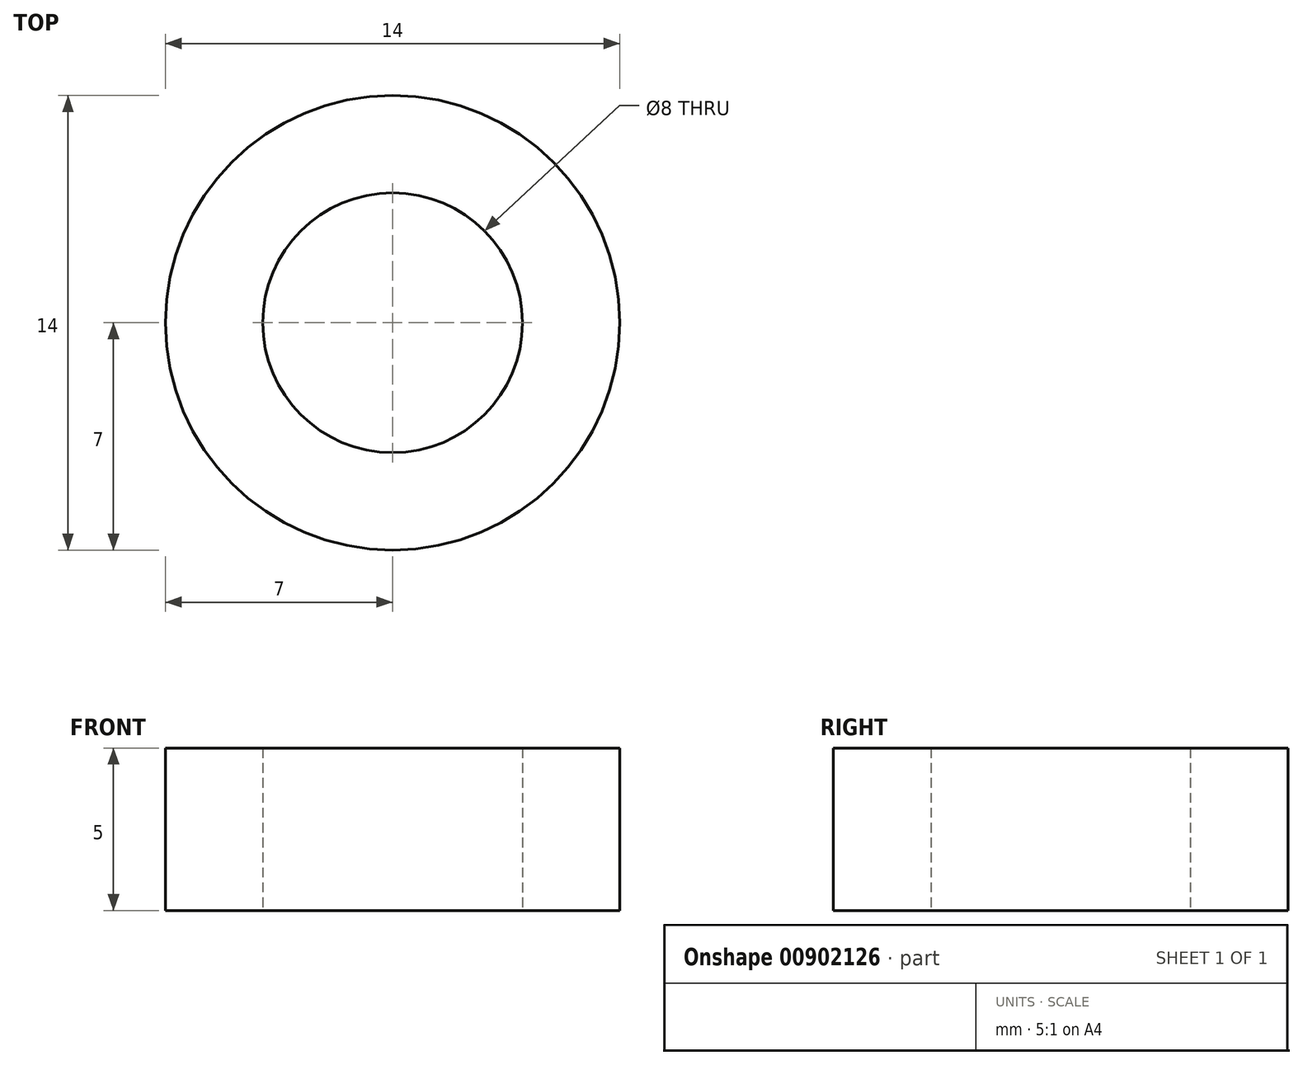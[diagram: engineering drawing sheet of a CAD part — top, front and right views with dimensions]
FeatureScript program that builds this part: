
annotation { "Feature Type Name" : "Feature", "Feature Type Description" : "" }
export const myFeature = defineFeature(function(context is Context, id is Id, definition is map)
    precondition{}
    {
        {
            var Q0;
            Q0=qCreatedBy(makeId("Top.planeOp"),FACE);
            var sketch = newSketch(context, id + "F0", { "sketchPlane" : qUnion([Q0])});
            skCircle(sketch, "E0", {"center": v(0, 0) * mm, "radius": 7 * mm});
            skCircle(sketch, "E1", {"center": v(0, 0) * mm, "radius": 4 * mm});
            skSolve(sketch);
        }
        {
            var Q0;
            Q0=makeQuery(id+"F0.imprint","IMPRINT",FACE,{"disambiguationData":[TD([[makeQuery(id+"F0.imprint","IMPRINT",EDGE,{"derivedFrom":sQuery(id+"F0.wireOp",EDGE,"E0")}),1.0]])]});
            extrude(context, id + "F1", {"entities" : qUnion([Q0]), "depth" : 5 * mm, "offsetDistance" : 25 * mm});
        }
    });
